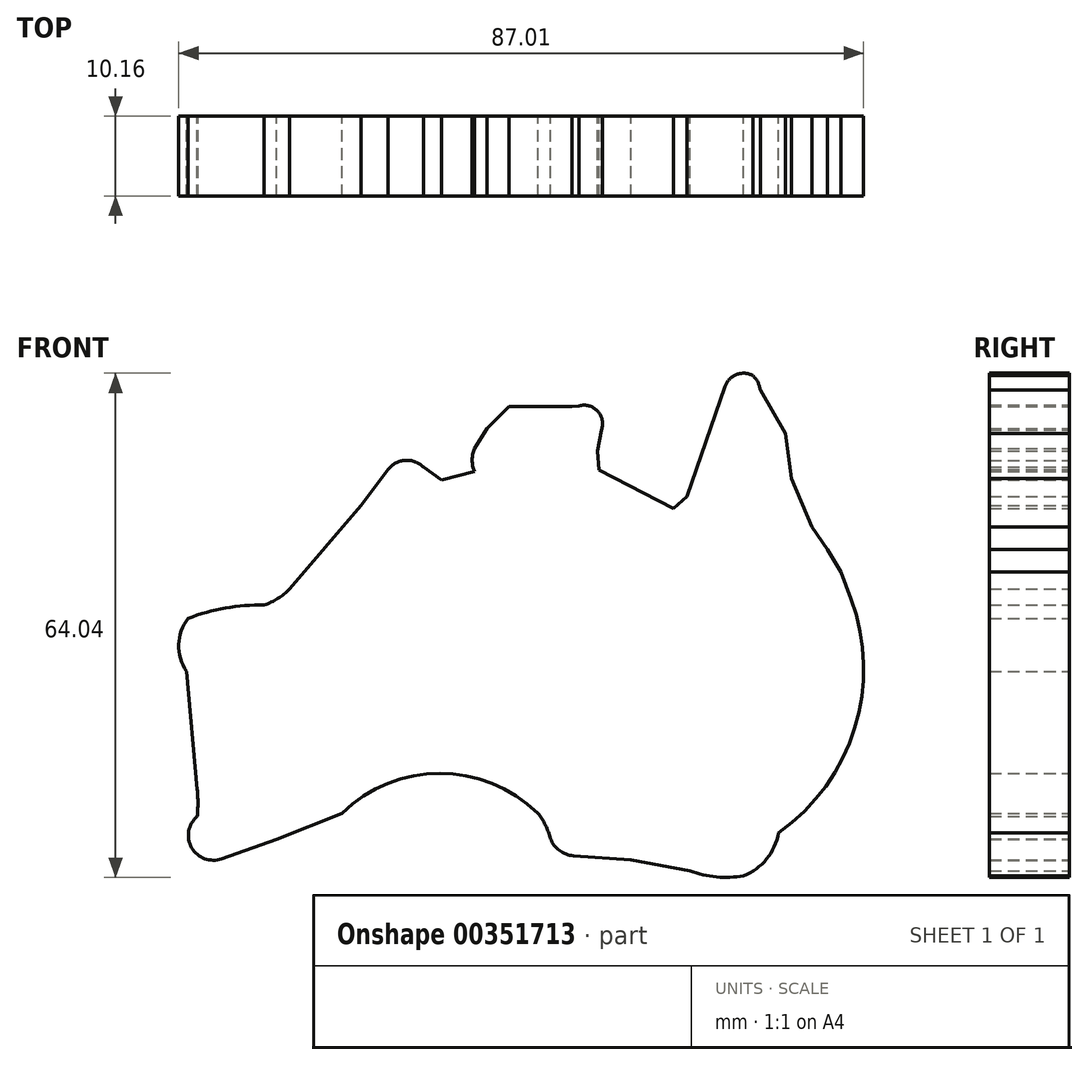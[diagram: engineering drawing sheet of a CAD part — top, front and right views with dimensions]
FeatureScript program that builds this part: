
annotation { "Feature Type Name" : "Feature", "Feature Type Description" : "" }
export const myFeature = defineFeature(function(context is Context, id is Id, definition is map)
    precondition{}
    {
        {
            var Q0;
            Q0=qCreatedBy(makeId("Front.planeOp"),FACE);
            var sketch = newSketch(context, id + "F0", { "sketchPlane" : qUnion([Q0])});
            skLineSegment(sketch, "E0", {"start": v(52.4, 71.53) * mm, "end": v(47.57, 57.55) * mm});
            skLineSegment(sketch, "E1", {"start": v(6.14, 56.41) * mm, "end": v(-2.93, 45.77) * mm});
            skLineSegment(sketch, "E2", {"start": v(-16.03, 35.32) * mm, "end": v(-14.65, 20.35) * mm});
            skPoint(sketch, "E3.2.internal.snap0", {"position": v(-15.34, 27.84) * mm});
            skLineSegment(sketch, "E4", {"start": v(36.4, 60.87) * mm, "end": v(45.84, 56.01) * mm});
            skLineSegment(sketch, "E5", {"start": v(45.84, 56.01) * mm, "end": v(47.57, 57.55) * mm});
            skArc(sketch, "E6", {"start": v(55.93, 72.88) * mm, "mid": v(53.85, 73.03) * mm, "end": v(52.4, 71.53) * mm});
            skArc(sketch, "E7", {"start": v(56.85, 71.08) * mm, "mid": v(56.55, 72.06) * mm, "end": v(55.93, 72.88) * mm});
            skLineSegment(sketch, "E8", {"start": v(56.85, 71.08) * mm, "end": v(60.07, 65.52) * mm});
            skLineSegment(sketch, "E9", {"start": v(60.07, 65.52) * mm, "end": v(60.8, 59.8) * mm});
            skLineSegment(sketch, "E10", {"start": v(63.42, 53.7) * mm, "end": v(65.36, 50.79) * mm});
            skLineSegment(sketch, "E11", {"start": v(67.14, 47.92) * mm, "end": v(68.4, 44.53) * mm});
            skLineSegment(sketch, "E12", {"start": v(60.8, 59.8) * mm, "end": v(63.42, 53.7) * mm});
            skLineSegment(sketch, "E13", {"start": v(65.36, 50.79) * mm, "end": v(67.14, 47.92) * mm});
            skArc(sketch, "E14", {"start": v(59.18, 14.8) * mm, "mid": v(68.85, 28.1) * mm, "end": v(68.4, 44.53) * mm});
            skArc(sketch, "E15", {"start": v(54.73, 9.33) * mm, "mid": v(57.67, 11.48) * mm, "end": v(59.18, 14.8) * mm});
            skArc(sketch, "E16", {"start": v(47.93, 10) * mm, "mid": v(51.28, 9.21) * mm, "end": v(54.73, 9.33) * mm});
            skLineSegment(sketch, "E17", {"start": v(47.93, 10) * mm, "end": v(40.47, 11.37) * mm});
            skLineSegment(sketch, "E18", {"start": v(40.47, 11.37) * mm, "end": v(33.14, 11.9) * mm});
            skArc(sketch, "E19", {"start": v(30.22, 14.05) * mm, "mid": v(31.37, 12.56) * mm, "end": v(33.14, 11.9) * mm});
            skArc(sketch, "E20", {"start": v(30.22, 14.05) * mm, "mid": v(29.59, 15.76) * mm, "end": v(28.6, 17.3) * mm});
            skArc(sketch, "E21", {"start": v(28.6, 17.3) * mm, "mid": v(16.16, 22.34) * mm, "end": v(3.72, 17.3) * mm});
            skLineSegment(sketch, "E22", {"start": v(3.72, 17.3) * mm, "end": v(-4.6, 13.98) * mm});
            skLineSegment(sketch, "E23", {"start": v(-4.6, 13.98) * mm, "end": v(-11.56, 11.5) * mm});
            skArc(sketch, "E24", {"start": v(-14.65, 16.9) * mm, "mid": v(-15.36, 12.9) * mm, "end": v(-11.56, 11.5) * mm});
            skArc(sketch, "E25", {"start": v(-14.65, 16.9) * mm, "mid": v(-14.58, 18.62) * mm, "end": v(-14.65, 20.35) * mm});
            skArc(sketch, "E26", {"start": v(-15.83, 42.04) * mm, "mid": v(-17.01, 38.71) * mm, "end": v(-16.03, 35.32) * mm});
            skArc(sketch, "E27", {"start": v(-6.15, 43.73) * mm, "mid": v(-11.07, 43.36) * mm, "end": v(-15.83, 42.04) * mm});
            skArc(sketch, "E28", {"start": v(-6.15, 43.73) * mm, "mid": v(-4.43, 44.57) * mm, "end": v(-2.93, 45.77) * mm});
            skLineSegment(sketch, "E29", {"start": v(6.14, 56.41) * mm, "end": v(9.6, 60.94) * mm});
            skArc(sketch, "E30", {"start": v(14.07, 61.26) * mm, "mid": v(11.77, 62.13) * mm, "end": v(9.6, 60.94) * mm});
            skLineSegment(sketch, "E31", {"start": v(14.07, 61.26) * mm, "end": v(16.35, 59.64) * mm});
            skLineSegment(sketch, "E32", {"start": v(16.35, 59.64) * mm, "end": v(20.55, 60.7) * mm});
            skArc(sketch, "E33", {"start": v(20.55, 63.6) * mm, "mid": v(20.27, 62.15) * mm, "end": v(20.55, 60.7) * mm});
            skLineSegment(sketch, "E34", {"start": v(20.55, 63.6) * mm, "end": v(22.17, 66.2) * mm});
            skLineSegment(sketch, "E35", {"start": v(22.17, 66.2) * mm, "end": v(24.92, 68.94) * mm});
            skLineSegment(sketch, "E36", {"start": v(24.92, 68.94) * mm, "end": v(32.94, 68.98) * mm});
            skArc(sketch, "E37", {"start": v(36.68, 66) * mm, "mid": v(36.19, 68.38) * mm, "end": v(33.84, 69.05) * mm});
            skLineSegment(sketch, "E38", {"start": v(32.41, 68.94) * mm, "end": v(33.84, 69.05) * mm});
            skLineSegment(sketch, "E39", {"start": v(36.68, 66) * mm, "end": v(36.16, 63.3) * mm});
            skLineSegment(sketch, "E40", {"start": v(36.16, 63.3) * mm, "end": v(36.4, 60.87) * mm});
            skSolve(sketch);
        }
        {
            var Q0;
            Q0=makeQuery(id+"F0.imprint","IMPRINT",FACE,{"disambiguationData":[TD([[makeQuery(id+"F0.imprint","IMPRINT",EDGE,{"derivedFrom":sQuery(id+"F0.wireOp",EDGE,"E0")}),1.0]])]});
            extrude(context, id + "F1", {"entities" : qUnion([Q0]), "depth" : 10.16 * mm});
        }
    });
